# Revit family: Furniture_Hooks-Hangers_hansgrohe_Joleena-Towel-ring-04786000_
name_source: partatom
category: Furniture
revit_build: Autodesk Revit 2015 (Build: 20140903_1530(x64)
units: mm (PartAtom-declared; Revit-internal decimal feet)

## types (1)
- Chrome 000
    BIMobject category = Hooks & Hangers
    BIMobject category code = furniture-hooks-hangers
    BIMobject main category = Furniture
    BIMobject main category code = furniture
    BOSUseNativeGeometries = 1
    Brand url = http://www.hansgrohe-int.com
    Default Elevation = 4' - 0"
    Design country = Germany
    Edition number = 1
    GTIN code = https://4059625203477
    IFC Classification = Furnishing Element
    Installation instructions = https://www.hansgrohe-usa.com
    Manufacturer country = Germany
    Manufacturer name = hansgrohe
    Masterformat 2014 Code = 41 23 19
    Masterformat 2014 Description = Hooks
    Material main = Chrome
    NBS Reference Code = 36-59-38
    NBS Reference Description = Holders And Hooks
    OmniClass Code = 23-31 25 25
    OmniClass Description = Towel Bars
    Product Guid = e3c58519-11c2-4358-a457-6e3a0786e132
    Product SKU = 04786000
    Product data url = https://bimobject.com
    Product family = Joleena
    Product group = Towel ring
    Product name = Joleena Towel ring 04786000
    Product url = https://www.hansgrohe-usa.com
    QR code = http://bimobject.com
    Technical description = https://www.hansgrohe-usa.com
    UNSPSC Code = 56
    Uniclass 1.4 Code = JN
    Uniclass 1.4 Description = Furniture/Equipment
    Uniclass 2.0 Code = PR-36-59-38
    Uniclass 2.0 Description = Holders And Hooks
    Uniclass 2015 Code = Pr_30_36_59_38
    Uniclass 2015 Name = Holders and hooks
    Uniformat II Code = E1090
    Uniformat II Description = Other Equipment

## geometry (parser evidence)
native form markers: Sweep x3
no freeform markers — native parametric forms only
